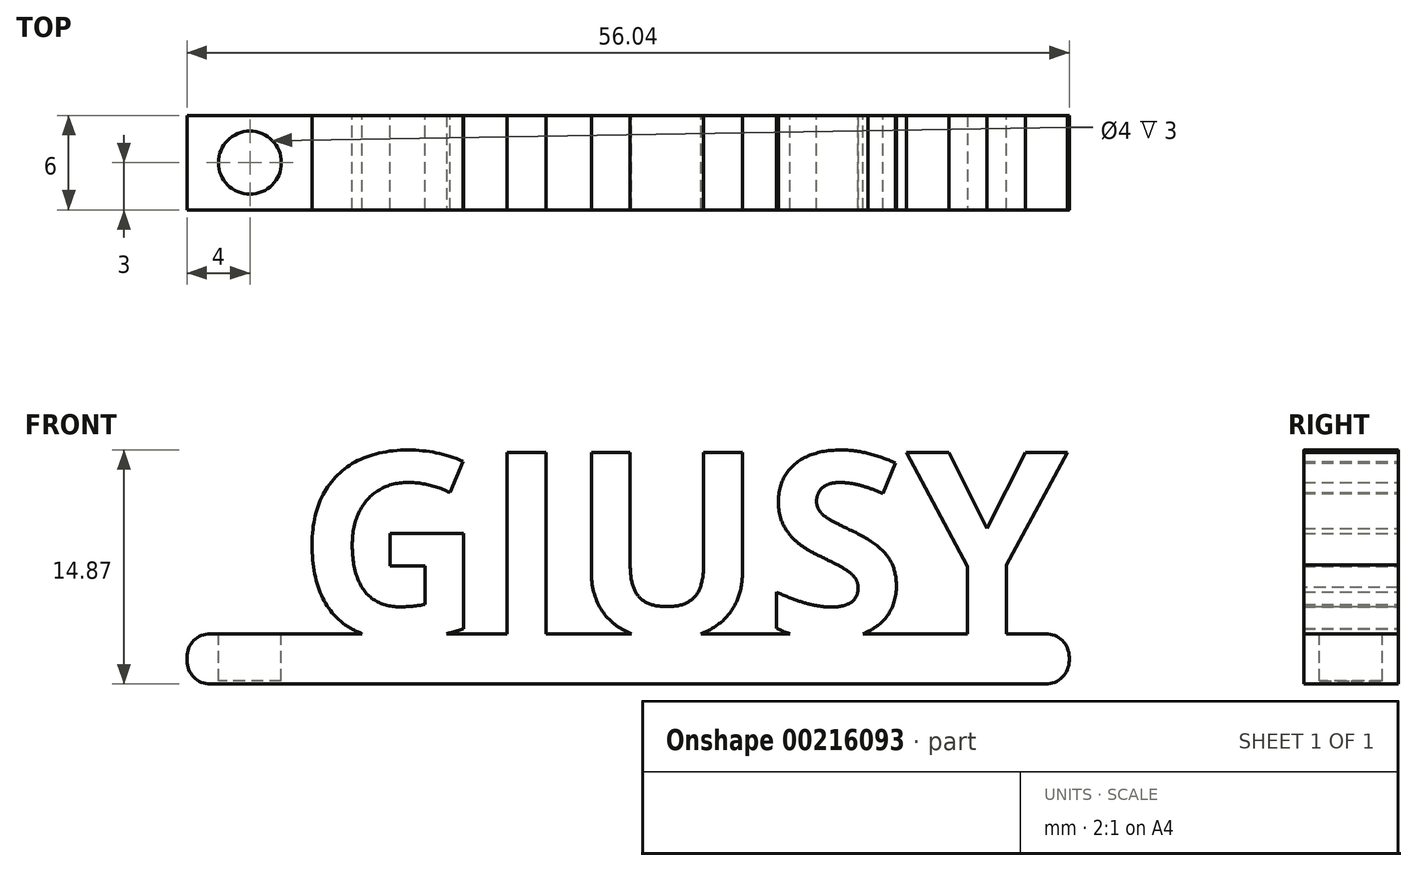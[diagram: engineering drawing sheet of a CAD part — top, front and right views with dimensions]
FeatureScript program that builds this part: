
annotation { "Feature Type Name" : "Feature", "Feature Type Description" : "" }
export const myFeature = defineFeature(function(context is Context, id is Id, definition is map)
    precondition{}
    {
        {
            var Q0;
            Q0=qCreatedBy(makeId("Front.planeOp"),FACE);
            var sketch = newSketch(context, id + "F0", { "sketchPlane" : qUnion([Q0])});
            skText(sketch, "E0", { "text": "GIUSY", "fontName": "OpenSans-Bold.ttf"});
            const initialGuessF0  = {"E0": [-0.02, 0, 1, 0, 0.0118]};
            skSetInitialGuess(sketch, initialGuessF0);
            skSolve(sketch);
        }
        {
            var Q0;
            Q0=qCreatedBy(makeId("Top.planeOp"),FACE);
            var sketch = newSketch(context, id + "F1", { "sketchPlane" : qUnion([Q0])});
            skLineSegment(sketch, "E1.bottom", {"start": v(-20, 3) * mm, "end": v(29.04, 3) * mm});
            skLineSegment(sketch, "E1.top", {"start": v(-20, -3) * mm, "end": v(29.04, -3) * mm});
            skLineSegment(sketch, "E1.left", {"start": v(-20, 3) * mm, "end": v(-20, -3) * mm});
            skLineSegment(sketch, "E1.right", {"start": v(29.04, 3) * mm, "end": v(29.04, -3) * mm});
            skSolve(sketch);
        }
        {
            var Q0;
            Q0=qSketchRegion(id+"F0",true);
            extrude(context, id + "F2", {"entities" : qUnion([Q0]), "endBound" : BoundingType.SYMMETRIC, "depth" : 6 * mm});
        }
        {
            var Q0;
            Q0=makeQuery(id+"F1.imprint","IMPRINT",FACE,{"disambiguationData":[TD([[makeQuery(id+"F1.imprint","IMPRINT",EDGE,{"derivedFrom":sQuery(id+"F1.wireOp",EDGE,"E1.bottom")}),-1.0]])]});
            extrude(context, id + "F3", {"entities" : qUnion([Q0]), "depth" : 0.2 * mm});
        }
        {
            var Q0;
            Q0=makeQuery(id+"F3.opExtrude","CAP_FACE",FACE,{"disambiguationData":[OSD([sQuery(id+"F1.wireOp",EDGE,"E1.bottom"),sQuery(id+"F1.wireOp",EDGE,"E1.top"),sQuery(id+"F1.wireOp",EDGE,"E1.left"),sQuery(id+"F1.wireOp",EDGE,"E1.right")])],"isStart":true});
            extrude(context, id + "F4", {"entities" : qUnion([Q0]), "depth" : 3 * mm});
        }
        {
            var Q0;
            Q0=makeQuery(id+"F3.opExtrude","SWEPT_BODY",BODY,{"disambiguationData":[OSD([sQuery(id+"F1.wireOp",EDGE,"E1.bottom"),sQuery(id+"F1.wireOp",EDGE,"E1.top"),sQuery(id+"F1.wireOp",EDGE,"E1.left"),sQuery(id+"F1.wireOp",EDGE,"E1.right")])]});
            var Q1;
            Q1=makeQuery(id+"F4.opExtrude","SWEPT_BODY",BODY,{"disambiguationData":[OSD([sQuery(id+"F1.wireOp",EDGE,"E1.bottom"),sQuery(id+"F1.wireOp",EDGE,"E1.top"),sQuery(id+"F1.wireOp",EDGE,"E1.left"),sQuery(id+"F1.wireOp",EDGE,"E1.right")])]});
            var Q2;
            Q2=makeQuery(id+"F2.opExtrude","SWEPT_BODY",BODY,{"disambiguationData":[OSD([sQuery(id+"F0.wireOp",EDGE,"E0.sketch_text.stroke-38"),sQuery(id+"F0.wireOp",EDGE,"E0.sketch_text.stroke-39"),sQuery(id+"F0.wireOp",EDGE,"E0.sketch_text.stroke-40"),sQuery(id+"F0.wireOp",EDGE,"E0.sketch_text.stroke-41"),sQuery(id+"F0.wireOp",EDGE,"E0.sketch_text.stroke-42"),sQuery(id+"F0.wireOp",EDGE,"E0.sketch_text.stroke-43"),sQuery(id+"F0.wireOp",EDGE,"E0.sketch_text.stroke-44"),sQuery(id+"F0.wireOp",EDGE,"E0.sketch_text.stroke-45"),sQuery(id+"F0.wireOp",EDGE,"E0.sketch_text.stroke-46"),sQuery(id+"F0.wireOp",EDGE,"E0.sketch_text.stroke-47"),sQuery(id+"F0.wireOp",EDGE,"E0.sketch_text.stroke-48"),sQuery(id+"F0.wireOp",EDGE,"E0.sketch_text.stroke-49"),sQuery(id+"F0.wireOp",EDGE,"E0.sketch_text.stroke-50"),sQuery(id+"F0.wireOp",EDGE,"E0.sketch_text.stroke-51"),sQuery(id+"F0.wireOp",EDGE,"E0.sketch_text.stroke-52"),sQuery(id+"F0.wireOp",EDGE,"E0.sketch_text.stroke-53"),sQuery(id+"F0.wireOp",EDGE,"E0.sketch_text.stroke-54"),sQuery(id+"F0.wireOp",EDGE,"E0.sketch_text.stroke-55"),sQuery(id+"F0.wireOp",EDGE,"E0.sketch_text.stroke-56"),sQuery(id+"F0.wireOp",EDGE,"E0.sketch_text.stroke-57"),sQuery(id+"F0.wireOp",EDGE,"E0.sketch_text.stroke-58"),sQuery(id+"F0.wireOp",EDGE,"E0.sketch_text.stroke-59"),sQuery(id+"F0.wireOp",EDGE,"E0.sketch_text.stroke-60"),sQuery(id+"F0.wireOp",EDGE,"E0.sketch_text.stroke-61"),sQuery(id+"F0.wireOp",EDGE,"E0.sketch_text.stroke-62"),sQuery(id+"F0.wireOp",EDGE,"E0.sketch_text.stroke-63"),sQuery(id+"F0.wireOp",EDGE,"E0.sketch_text.stroke-64"),sQuery(id+"F0.wireOp",EDGE,"E0.sketch_text.stroke-65")])]});
            var Q3;
            Q3=makeQuery(id+"F2.opExtrude","SWEPT_BODY",BODY,{"disambiguationData":[OSD([sQuery(id+"F0.wireOp",EDGE,"E0.sketch_text.stroke-19"),sQuery(id+"F0.wireOp",EDGE,"E0.sketch_text.stroke-20"),sQuery(id+"F0.wireOp",EDGE,"E0.sketch_text.stroke-21"),sQuery(id+"F0.wireOp",EDGE,"E0.sketch_text.stroke-22")])]});
            var Q4;
            Q4=makeQuery(id+"F2.opExtrude","SWEPT_BODY",BODY,{"disambiguationData":[OSD([sQuery(id+"F0.wireOp",EDGE,"E0.sketch_text.stroke-0"),sQuery(id+"F0.wireOp",EDGE,"E0.sketch_text.stroke-1"),sQuery(id+"F0.wireOp",EDGE,"E0.sketch_text.stroke-2"),sQuery(id+"F0.wireOp",EDGE,"E0.sketch_text.stroke-3"),sQuery(id+"F0.wireOp",EDGE,"E0.sketch_text.stroke-4"),sQuery(id+"F0.wireOp",EDGE,"E0.sketch_text.stroke-5"),sQuery(id+"F0.wireOp",EDGE,"E0.sketch_text.stroke-6"),sQuery(id+"F0.wireOp",EDGE,"E0.sketch_text.stroke-7"),sQuery(id+"F0.wireOp",EDGE,"E0.sketch_text.stroke-8"),sQuery(id+"F0.wireOp",EDGE,"E0.sketch_text.stroke-9"),sQuery(id+"F0.wireOp",EDGE,"E0.sketch_text.stroke-10"),sQuery(id+"F0.wireOp",EDGE,"E0.sketch_text.stroke-11"),sQuery(id+"F0.wireOp",EDGE,"E0.sketch_text.stroke-12"),sQuery(id+"F0.wireOp",EDGE,"E0.sketch_text.stroke-13"),sQuery(id+"F0.wireOp",EDGE,"E0.sketch_text.stroke-14"),sQuery(id+"F0.wireOp",EDGE,"E0.sketch_text.stroke-15"),sQuery(id+"F0.wireOp",EDGE,"E0.sketch_text.stroke-16"),sQuery(id+"F0.wireOp",EDGE,"E0.sketch_text.stroke-17"),sQuery(id+"F0.wireOp",EDGE,"E0.sketch_text.stroke-18")])]});
            var Q5;
            Q5=makeQuery(id+"F2.opExtrude","SWEPT_BODY",BODY,{"disambiguationData":[OSD([sQuery(id+"F0.wireOp",EDGE,"E0.sketch_text.stroke-66"),sQuery(id+"F0.wireOp",EDGE,"E0.sketch_text.stroke-67"),sQuery(id+"F0.wireOp",EDGE,"E0.sketch_text.stroke-68"),sQuery(id+"F0.wireOp",EDGE,"E0.sketch_text.stroke-69"),sQuery(id+"F0.wireOp",EDGE,"E0.sketch_text.stroke-70"),sQuery(id+"F0.wireOp",EDGE,"E0.sketch_text.stroke-71"),sQuery(id+"F0.wireOp",EDGE,"E0.sketch_text.stroke-72"),sQuery(id+"F0.wireOp",EDGE,"E0.sketch_text.stroke-73"),sQuery(id+"F0.wireOp",EDGE,"E0.sketch_text.stroke-74")])]});
            var Q6;
            Q6=makeQuery(id+"F2.opExtrude","SWEPT_BODY",BODY,{"disambiguationData":[OSD([sQuery(id+"F0.wireOp",EDGE,"E0.sketch_text.stroke-23"),sQuery(id+"F0.wireOp",EDGE,"E0.sketch_text.stroke-24"),sQuery(id+"F0.wireOp",EDGE,"E0.sketch_text.stroke-25"),sQuery(id+"F0.wireOp",EDGE,"E0.sketch_text.stroke-26"),sQuery(id+"F0.wireOp",EDGE,"E0.sketch_text.stroke-27"),sQuery(id+"F0.wireOp",EDGE,"E0.sketch_text.stroke-28"),sQuery(id+"F0.wireOp",EDGE,"E0.sketch_text.stroke-29"),sQuery(id+"F0.wireOp",EDGE,"E0.sketch_text.stroke-30"),sQuery(id+"F0.wireOp",EDGE,"E0.sketch_text.stroke-31"),sQuery(id+"F0.wireOp",EDGE,"E0.sketch_text.stroke-32"),sQuery(id+"F0.wireOp",EDGE,"E0.sketch_text.stroke-33"),sQuery(id+"F0.wireOp",EDGE,"E0.sketch_text.stroke-34"),sQuery(id+"F0.wireOp",EDGE,"E0.sketch_text.stroke-35"),sQuery(id+"F0.wireOp",EDGE,"E0.sketch_text.stroke-36"),sQuery(id+"F0.wireOp",EDGE,"E0.sketch_text.stroke-37")])]});
            booleanBodies(context, id + "F5", {"operationType" : BooleanOperationType.UNION, "tools" : qUnion([Q0, Q1, Q2, Q3, Q4, Q5, Q6])});
        }
        {
            var Q0;
            {var subQ0=sQuery(id+"F1.wireOp",EDGE,"E1.left");Q0=makeQuery(id+"F5.opBoolean","MERGE",FACE,{"derivedFrom":[makeQuery(id+"F3.opExtrude","SWEPT_FACE",FACE,{"disambiguationData":[OSD([subQ0])]}),makeQuery(id+"F4.opExtrude","SWEPT_FACE",FACE,{"disambiguationData":[OSD([subQ0])]})]});}
            var sketch = newSketch(context, id + "F6", { "sketchPlane" : qUnion([Q0])});
            skLineSegment(sketch, "E2.bottom", {"start": v(-3, -3) * mm, "end": v(3, -3) * mm});
            skLineSegment(sketch, "E2.top", {"start": v(-3, 0.2) * mm, "end": v(3, 0.2) * mm});
            skLineSegment(sketch, "E2.left", {"start": v(-3, -3) * mm, "end": v(-3, 0.2) * mm});
            skLineSegment(sketch, "E2.right", {"start": v(3, -3) * mm, "end": v(3, 0.2) * mm});
            skSolve(sketch);
        }
        {
            var Q0;
            Q0=qSketchRegion(id+"F6",true);
            extrude(context, id + "F7", {"entities" : qUnion([Q0]), "operationType" : NewBodyOperationType.ADD, "depth" : 7 * mm});
        }
        {
            var Q0;
            Q0=makeQuery(id+"F7.opExtrude","CAP_EDGE",EDGE,{"disambiguationData":[OSD([sQuery(id+"F6.wireOp",EDGE,"E2.bottom")])],"isStart":false});
            var Q1;
            Q1=makeQuery(id+"F7.opExtrude","CAP_EDGE",EDGE,{"disambiguationData":[OSD([sQuery(id+"F6.wireOp",EDGE,"E2.top")])],"isStart":false});
            var Q2;
            Q2=makeQuery(id+"F4.opExtrude","CAP_EDGE",EDGE,{"disambiguationData":[OSD([sQuery(id+"F1.wireOp",EDGE,"E1.right")])],"isStart":false});
            var Q3;
            Q3=makeQuery(id+"F3.opExtrude","CAP_EDGE",EDGE,{"disambiguationData":[OSD([sQuery(id+"F1.wireOp",EDGE,"E1.right")])],"isStart":false});
            fillet(context, id + "F8", {"entities" : qUnion([Q0, Q1, Q2, Q3]), "radius" : 1.5 * mm, "tangentPropagation" : true, "allowEdgeOverflow" : false});
        }
        {
            var Q0;
            {var subQ19=sQuery(id+"F1.wireOp",EDGE,"E1.top");var subQ20=sQuery(id+"F1.wireOp",EDGE,"E1.bottom");var subQ63=sQuery(id+"F0.wireOp",EDGE,"E0.sketch_text.stroke-2");var subQ66=sQuery(id+"F1.wireOp",EDGE,"E1.left");Q0=makeQuery(id+"F7.boolean.opBoolean","MERGE",FACE,{"derivedFrom":[makeQuery(id+"F5.opBoolean","SPLIT",FACE,{"disambiguationData":[TD([makeQuery(id+"F2.opExtrude","SWEPT_FACE",FACE,{"disambiguationData":[OSD([subQ63])]})])],"derivedFrom":makeQuery(id+"F3.opExtrude","CAP_FACE",FACE,{"disambiguationData":[OSD([subQ20,subQ19,subQ66,sQuery(id+"F1.wireOp",EDGE,"E1.right")])],"isStart":false})}),makeQuery(id+"F7.opExtrude","SWEPT_FACE",FACE,{"disambiguationData":[OSD([sQuery(id+"F6.wireOp",EDGE,"E2.top")])]})]});}
            var sketch = newSketch(context, id + "F9", { "sketchPlane" : qUnion([Q0])});
            skCircle(sketch, "E3", {"center": v(-23, 0) * mm, "radius": 2 * mm});
            skSolve(sketch);
        }
        {
            var Q0;
            Q0=makeQuery(id+"F9.imprint","IMPRINT",FACE,{"disambiguationData":[TD([[makeQuery(id+"F9.imprint","IMPRINT",EDGE,{"derivedFrom":sQuery(id+"F9.wireOp",EDGE,"E3")}),1.0]])]});
            extrude(context, id + "F10", {"entities" : qUnion([Q0]), "operationType" : NewBodyOperationType.REMOVE, "oppositeDirection" : true, "depth" : 3 * mm});
        }
    });
